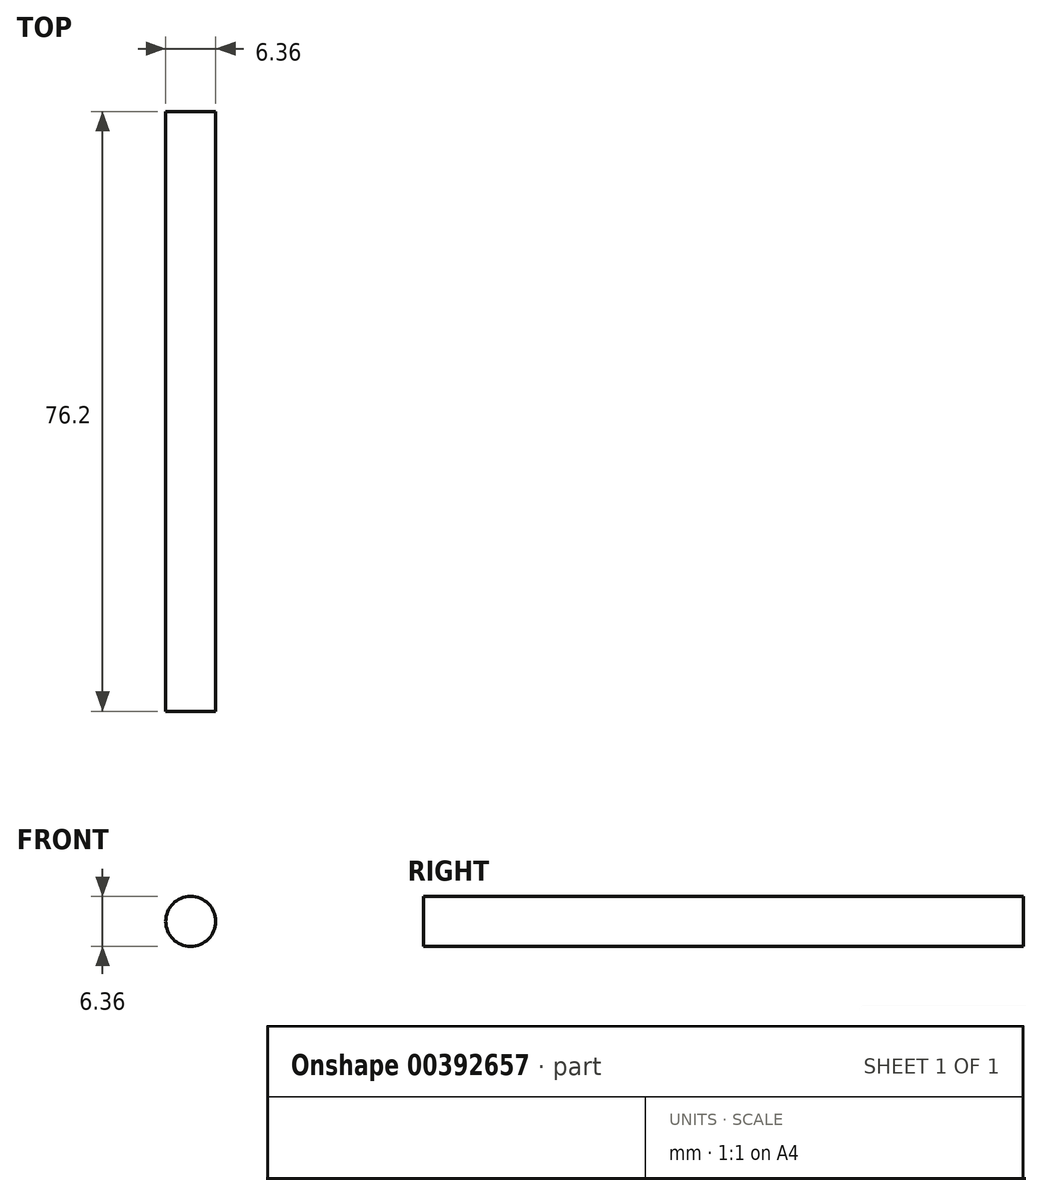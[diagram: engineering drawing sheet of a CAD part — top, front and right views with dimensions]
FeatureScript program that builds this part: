
annotation { "Feature Type Name" : "Feature", "Feature Type Description" : "" }
export const myFeature = defineFeature(function(context is Context, id is Id, definition is map)
    precondition{}
    {
        {
            var Q0;
            Q0=qCreatedBy(makeId("Front.planeOp"),FACE);
            var sketch = newSketch(context, id + "F0", { "sketchPlane" : qUnion([Q0])});
            skCircle(sketch, "E0", {"center": v(0, 0) * mm, "radius": 3.18 * mm});
            skSolve(sketch);
        }
        {
            var Q0;
            Q0=makeQuery(id+"F0.imprint","IMPRINT",FACE,{"disambiguationData":[TD([[makeQuery(id+"F0.imprint","IMPRINT",EDGE,{"derivedFrom":sQuery(id+"F0.wireOp",EDGE,"E0")}),1.0]])]});
            extrude(context, id + "F1", {"entities" : qUnion([Q0]), "oppositeDirection" : true, "depth" : 76.2 * mm});
        }
    });
